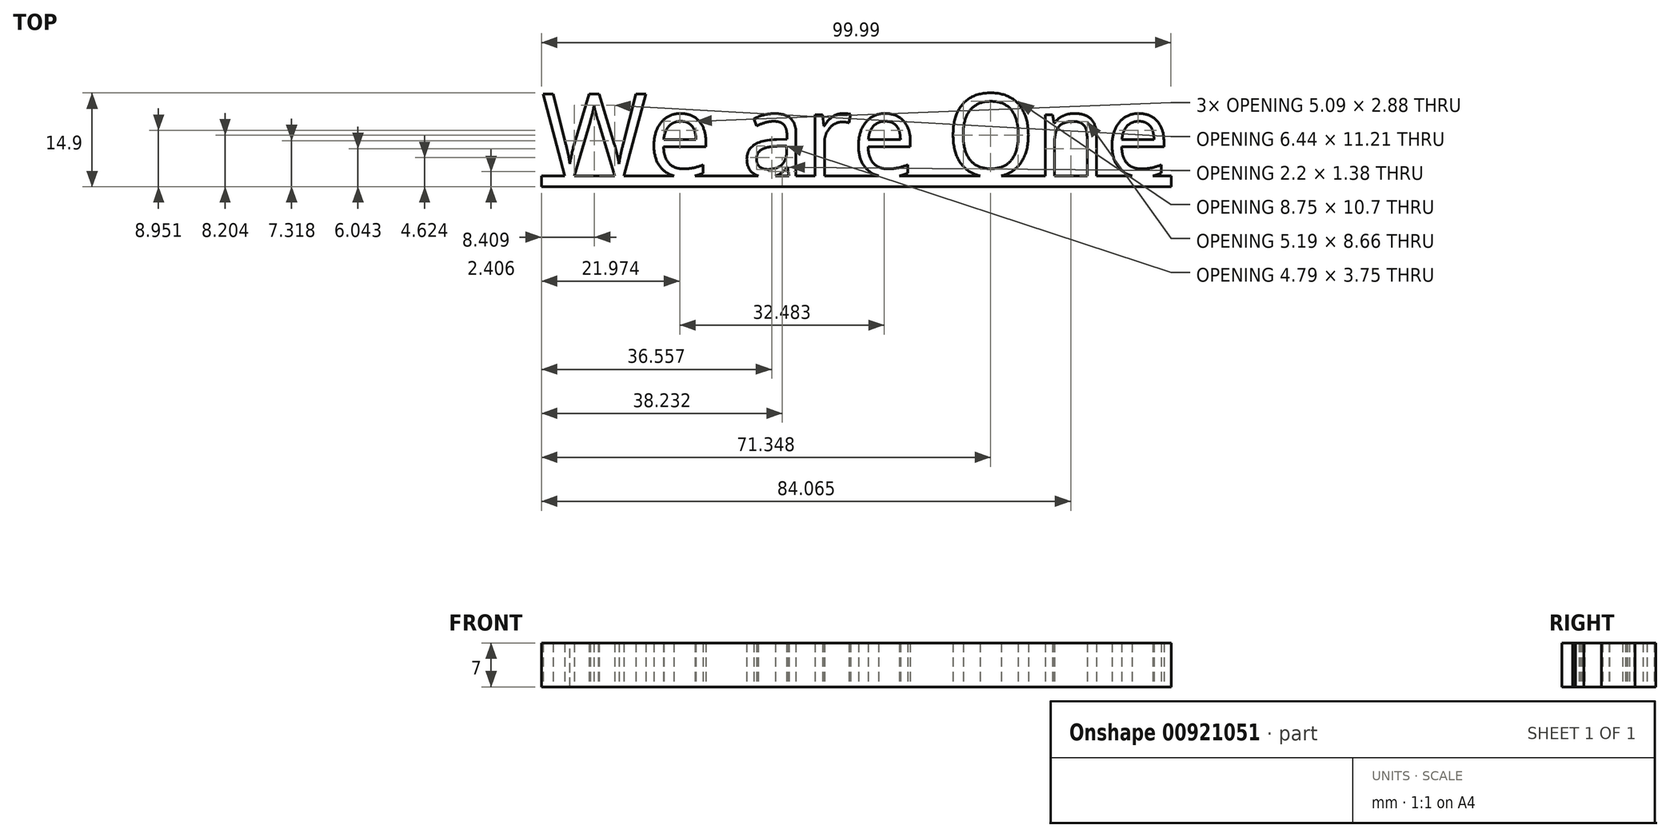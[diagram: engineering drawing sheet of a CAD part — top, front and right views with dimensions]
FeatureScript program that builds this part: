
annotation { "Feature Type Name" : "Feature", "Feature Type Description" : "" }
export const myFeature = defineFeature(function(context is Context, id is Id, definition is map)
    precondition{}
    {
        {
            var Q0;
            Q0=qCreatedBy(makeId("Top.planeOp"),FACE);
            var sketch = newSketch(context, id + "F0", { "sketchPlane" : qUnion([Q0])});
            skText(sketch, "E0", { "text": "We are One", "fontName": "OpenSans-Regular.ttf"});
            skLineSegment(sketch, "E1.bottom", {"start": v(15.26, -13.1) * mm, "end": v(86.24, -13.1) * mm});
            skLineSegment(sketch, "E2.bottom", {"start": v(0, -13.1) * mm, "end": v(100, -13.1) * mm});
            skLineSegment(sketch, "E2.top", {"start": v(0, -14.81) * mm, "end": v(100, -14.81) * mm});
            skLineSegment(sketch, "E2.left", {"start": v(0, -13.1) * mm, "end": v(0, -14.81) * mm});
            skLineSegment(sketch, "E2.right", {"start": v(100, -13.1) * mm, "end": v(100, -14.81) * mm});
            const initialGuessF0  = {"E0": [0, -0.0131, 1, 0, 0.0131]};
            skSetInitialGuess(sketch, initialGuessF0);
            skSolve(sketch);
        }
        {
            var Q0;
            Q0 = qSketchRegion(id + "F0", true);
            extrude(context, id + "F1", {"entities" : qUnion([Q0]), "depth" : 7 * mm, "offsetDistance" : 25 * mm});
        }
    });
